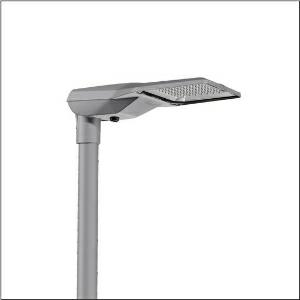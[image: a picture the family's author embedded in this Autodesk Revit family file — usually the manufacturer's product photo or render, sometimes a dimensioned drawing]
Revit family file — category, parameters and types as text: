
# Revit family: streetlight_sl_21_iq_midi___p0_8a_5xe3u31u08mb_6097
name_source: partatom
category: Lighting Fixtures
units: mm (PartAtom-declared; Revit-internal decimal feet)

## family parameters
Cut with Voids When Loaded = No
Host = Face
Light Source = No
Part Type = Normal
Room Calculation Point = No
Round Connector Dimension = Use Diameter
Shared = No

## types (1)
- --- (1 x LED, 18500 lm, 129.3 W, 3000K)
    Apparent Load = 129 VA
    CIE Flux Codes = 33 69 96 100 100
    Color Rendering = 70
    Color Temperature = 3000K
    Default Elevation = 1800 mm
    Description = Streetlight SL 21 iQ midi, mast luminaire, primary light control with lens, of PMMA, primary optical cover: cover, of toughened safety glass, transparent, light distribution: P0.8a, light emission: direct distribution, primary light characteristic: asymmetric, installation type: post-top, side-entry, LED, High Power LED, rated luminous flux: 18.500lm, luminous efficacy: 143lm/W, light colour: 730, colour temperature: 3000K, control gear: iQ-Street Remote, D4i with power reduction, control: pre-setting: logarithmic dimming characteristic, Street-Remote, Auto-Match, Temp-Guard, Lumen-Switch, Night-Set, Smart-Wire, Light-Fading, Desk-Remote (wireless, voltage-free reading and setting of iQ features in the workshop via application-optimized NFC function/RFID function), optimised constant luminous flux control (CLO 2.0), mains connection: 230..240V, AC, 50/60Hz, start of lifetime: 129W, end of service life: 142W, reduction: 56W, luminaire housing, of diecast aluminium, powder-coated, Siteco® metallic grey (DB 702S), corrosivity category C5 mid according to DIN EN ISO 12944, please order mast flange separately, inclination adjustable: 0°, 5°, 10°, 15°, sealing non-destructively replaceable, multi-level sealing system, length: 644mm, width: 335mm, height: 110mm, mast flange for spigot size: 42mm (side-entry): 5XC10008XM4, 60/48mm (side-entry/post-top): 5XC10108XM2, 76/60mm (side-entry/post-top): 5XC10108XM1, mounting height: 4..8m, Smart Interface below, protection rating (complete): IP66, insulation class (complete): insulation class II (safety insulation), certification: CE, ENEC, ENEC+, VDE, impact resistance: IK10, permissible operating ambient temperature for outdoor applications: -40..+50°C, standard-compliant lighting for roads and squares, packaging unit: 1 piece

Light Distribution: P0.8a
    Height = 111 mm
    Lamp = 1 x LED
    Lamp Light Flux = 18500 lm
    Lamp Power = 129.3 W
    Lamp count = 1
    Length = 644 mm
    Luminous efficacy = 143 lm/W
    Manufacturer = Siteco
    ModVariant = No
    Model = 5XE3U31U08MB
    Number of Poles = 1
    OnlyDefault = Yes
    Power Factor = 1
    Product Name = Streetlight SL 21 iQ midi | P0.8a
    Product group = mast luminaire | pylon top
    ProductGroupID = 6100
    Protection Class = Protection class II
    Protection Degree = IP 66
    RLX_Detail_Level = 1
    RLX_Emergency_Light_Flux = 0 lm
    RLX_Emergency_Type = 0
    RLX_Emergency_Type_DB = No
    RlxData = <blob elided: 26969 chars, md5=43ef1e81>
    Socket = socket
    Standby Power = 0 W
    System Light Flux = 18500 lm
    System Power = 129 W
    Type Comments = factory setting: luminous flux: 100 % | dim-lin: 254 | 672 mA
    Type Image = l_1004300.jpg
    URL = http://relux.com
    VarID = @adj_073984
    Voltage = 0 V
    Weight = 0.00 kg
    Width = 336 mm

## geometry (parser evidence)
native form markers: Blend x4, Sweep x12
no freeform markers — native parametric forms only
